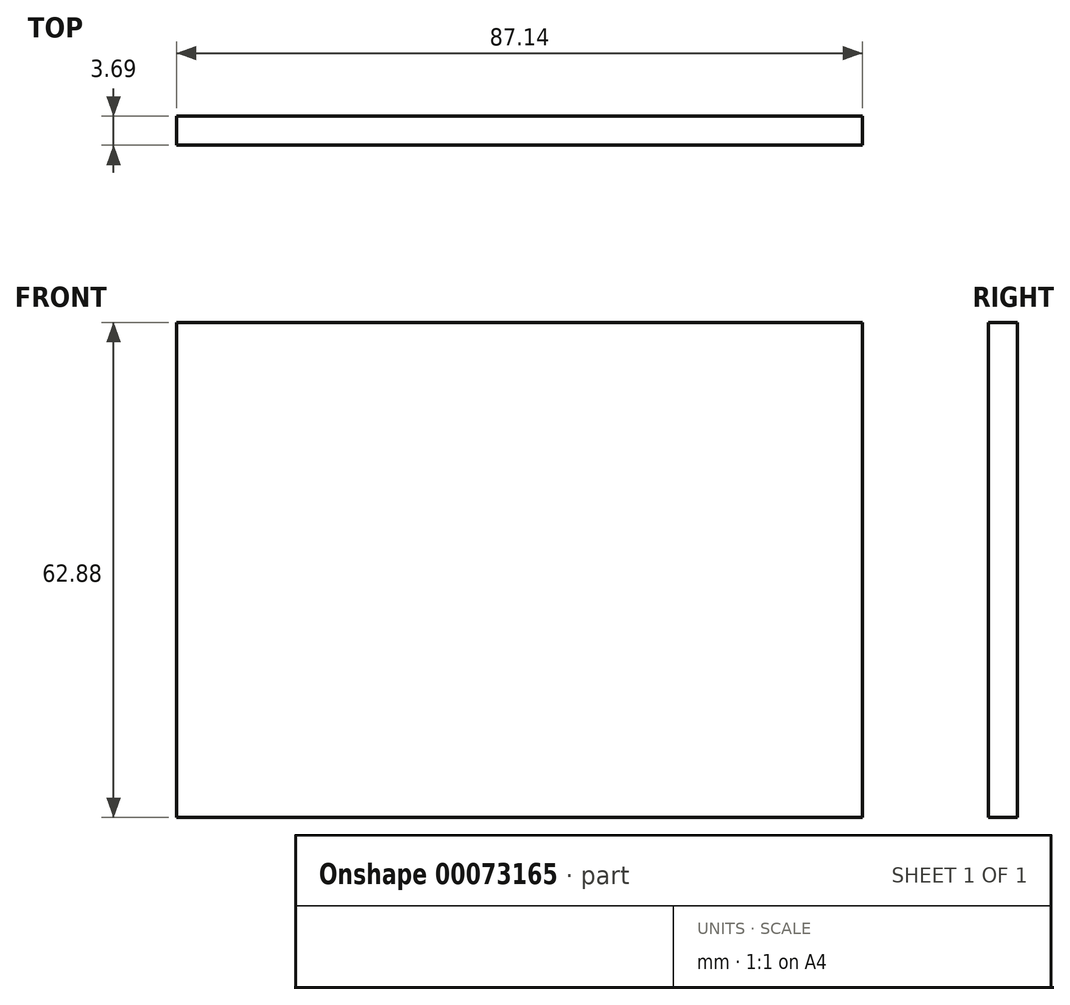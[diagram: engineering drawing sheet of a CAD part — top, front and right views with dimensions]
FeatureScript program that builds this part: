
annotation { "Feature Type Name" : "Feature", "Feature Type Description" : "" }
export const myFeature = defineFeature(function(context is Context, id is Id, definition is map)
    precondition{}
    {
        {
            var Q0;
            Q0=qCreatedBy(makeId("Front.planeOp"),FACE);
            var sketch = newSketch(context, id + "F0", { "sketchPlane" : qUnion([Q0])});
            skLineSegment(sketch, "E0.rect.bottom", {"start": v(43.57, -31.44) * mm, "end": v(-43.57, -31.44) * mm});
            skLineSegment(sketch, "E0.rect.top", {"start": v(43.57, 31.44) * mm, "end": v(-43.57, 31.44) * mm});
            skLineSegment(sketch, "E0.rect.left", {"start": v(43.57, -31.44) * mm, "end": v(43.57, 31.44) * mm});
            skLineSegment(sketch, "E0.rect.right", {"start": v(-43.57, -31.44) * mm, "end": v(-43.57, 31.44) * mm});
            skPoint(sketch, "E0.rect.middle", {"position": v(0, 0) * mm});
            skLineSegment(sketch, "E1.bottom", {"start": v(-22.6, -31.44) * mm, "end": v(18.6, -31.44) * mm});
            skLineSegment(sketch, "E1.top", {"start": v(-22.6, 0) * mm, "end": v(18.6, 0) * mm});
            skLineSegment(sketch, "E1.left", {"start": v(-22.6, -31.44) * mm, "end": v(-22.6, 0) * mm});
            skLineSegment(sketch, "E1.right", {"start": v(18.6, -31.44) * mm, "end": v(18.6, 0) * mm});
            skLineSegment(sketch, "E2.0", {"start": v(18.77, -31.44) * mm, "end": v(18.77, 0.18) * mm});
            skLineSegment(sketch, "E2.1", {"start": v(-22.79, 0.18) * mm, "end": v(18.77, 0.18) * mm});
            skLineSegment(sketch, "E2.2", {"start": v(-22.79, -35.9) * mm, "end": v(-22.79, 0.18) * mm});
            skSolve(sketch);
        }
        {
            var Q0;
            Q0 = qSketchRegion(id + "F0", true);
            extrude(context, id + "F1", {"entities" : qUnion([Q0]), "depth" : 3.7 * mm});
        }
    });
